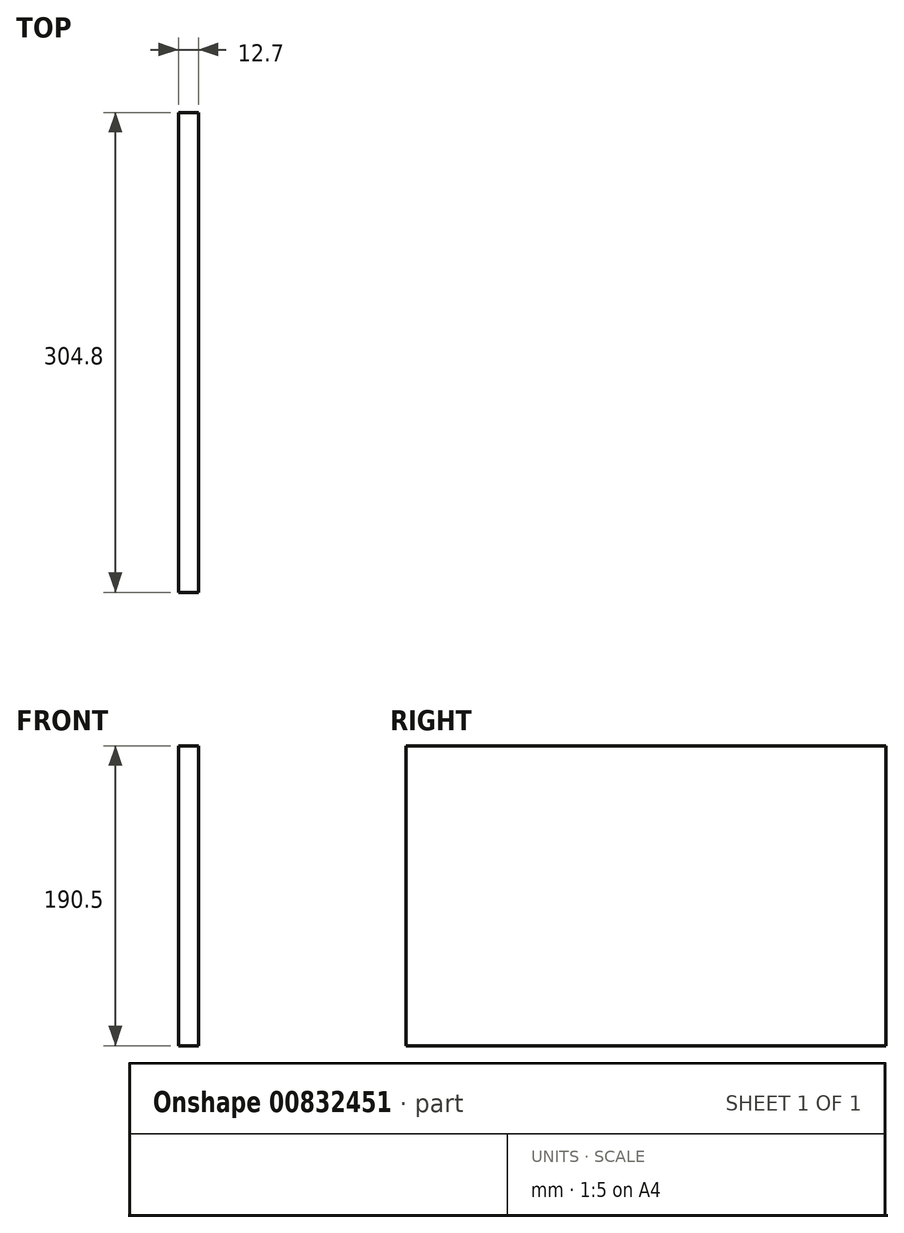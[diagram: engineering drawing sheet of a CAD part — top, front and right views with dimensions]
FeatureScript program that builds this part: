
annotation { "Feature Type Name" : "Feature", "Feature Type Description" : "" }
export const myFeature = defineFeature(function(context is Context, id is Id, definition is map)
    precondition{}
    {
        {
            var Q0;
            Q0=qCreatedBy(makeId("Front.planeOp"),FACE);
            var sketch = newSketch(context, id + "F0", { "sketchPlane" : qUnion([Q0])});
            skLineSegment(sketch, "E0.bottom", {"start": v(6.35, -95.25) * mm, "end": v(-6.35, -95.25) * mm});
            skLineSegment(sketch, "E0.top", {"start": v(6.35, 95.25) * mm, "end": v(-6.35, 95.25) * mm});
            skLineSegment(sketch, "E0.left", {"start": v(6.35, -95.25) * mm, "end": v(6.35, 95.25) * mm});
            skLineSegment(sketch, "E0.right", {"start": v(-6.35, -95.25) * mm, "end": v(-6.35, 95.25) * mm});
            skPoint(sketch, "E0.middle", {"position": v(0, 0) * mm});
            skSolve(sketch);
        }
        {
            var Q0;
            Q0=makeQuery(id+"F0.imprint","IMPRINT",FACE,{"disambiguationData":[TD([[makeQuery(id+"F0.imprint","IMPRINT",EDGE,{"derivedFrom":sQuery(id+"F0.wireOp",EDGE,"E0.bottom")}),-1.0]])]});
            extrude(context, id + "F1", {"entities" : qUnion([Q0]), "depth" : 304.8 * mm, "offsetDistance" : 25.4 * mm});
        }
    });
